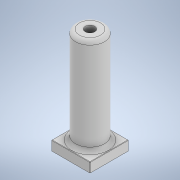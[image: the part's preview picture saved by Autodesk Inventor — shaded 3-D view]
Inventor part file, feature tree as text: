
AUTODESK INVENTOR PART (.ipt)
format: ipt  version: 2021.4 (Build 254397000, 397)  size: 145,920 bytes
history: native  units: mm
features: extrude x2, fillet x2, sketch x2, other x1
ambient origin geometry x8: Origin, YZ Plane, XZ Plane, XY Plane, X Axis, Y Axis, Z Axis, Center Point
bodies: Body1 (feature_tree)
feature tree (7):
  other  "ソリッド1"
  extrude  "押し出し1"  Depth=20.0mm
  fillet  "フィレット1"  Radius=20.0mm
  extrude  "押し出し2"  Depth=5.0mm TaperAngle=0.0deg
  fillet  "フィレット2"  Radius=0.2mm
  sketch  "スケッチ1"
  sketch  "スケッチ2"
